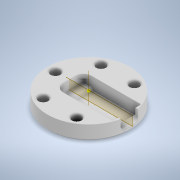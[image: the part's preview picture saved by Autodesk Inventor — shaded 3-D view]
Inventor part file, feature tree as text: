
AUTODESK INVENTOR PART (.ipt)
format: ipt  version: 2021 (Build 250183000, 183)  size: 815,104 bytes
history: native  units: in
note: dims shown in document units (in); Inventor stores cm internally (conversion verified against a paired STEP export)
features: sketch x8, extrude x6, fillet x4, chamfer x3, other x1, plane x1, pattern_circular x1, mirror x1
ambient origin geometry x8: Origin, YZ Plane, XZ Plane, XY Plane, X Axis, Y Axis, Z Axis, Center Point
bodies: Solid1 (feature_tree)
feature tree (25):
  extrude  "Extrusion1"  Depth=0.3701in TaperAngle=0.0deg
  chamfer  "Chamfer2"  Distance=0.2441in
  extrude  "Extrusion2"  Depth=0.1417in
  extrude  "Extrusion3"  Depth=0.2181in
  other  "Work Axis1"
  plane  "Work Plane1"
  extrude  "Extrusion5"  Depth=0.8268in
  extrude  "Extrusion4"  Depth=0.3539in
  fillet  "Fillet4"  Radius=0.1969in
  pattern_circular  "Circular Pattern2"  [2 undecoded]
  fillet  "Fillet7"  Radius=0.1417in
  extrude  "Initals"  TaperAngle=0.0deg  [1 undecoded]
  fillet  "Fillet9"  [1 undecoded]
  fillet  "Fillet10"  Radius=0.0394in
  mirror  "Mirror6"
  sketch  "Sketch18"  dims[d18=0.2047in d19=0.0in d23=0.8268in d24=0.3539in d31=0.1969in d32=0.063in d33=0.0in d44=0.1417in d47=0.0in d48=0.0in d49=0.0in d51=0.0in d54=0.0551in d55=0.0in d56=45.0deg d58=0.0394in d59=0.1181in d60=1.9685in d61=240.0deg d72=0.0315in d80=1.1811in d81=0.5906in d82=0.9728in d83=0.4864in d84=0.0394in d85=0.0in d86=0.547in d87=0.2735in d88=0.0787in d89=0.0in d90=0.0787in d98=0.1024in d99=0.0in d100=0.0in d101=0.2362in d102=0.0315in d103=0.0315in d104=0.2953in d105=0.1575in d106=0.1969in d107=0.063in d108=0.0787in d109=45.0deg d110=0.063in d111=0.0787in d112=45.0deg d91=0.0197in d92=0.0344in d93=0.0197in d94=0.0344in d120=0.0197in d121=0.0344in d122=0.0197in d123=0.0344in]
  chamfer  "Chamfer4"  Distance=0.1181in Angle=240.0deg
  chamfer  "Chamfer5"  Distance=0.0315in
  sketch  "Sketch1"  dims[d0=2.0472in d3=0.3701in d4=0.0in]
  sketch  "Sketch2"  dims[d5=1.4315in]
  sketch  "Sketch3"  dims[d6=0.7079in]
  sketch  "Sketch4"  dims[d7=0.3539in]
  sketch  "Sketch7"  dims[d8=0.4882in d9=0.2441in d10=0.0in]
  sketch  "Sketch12"  dims[d11=0.0in d14=0.1417in]
  sketch  "Sketch13"  dims[d15=0.0in d16=0.0in d17=0.2181in]
note: 4 required parameter values undecoded (feature->parameter linkage not recoverable at this tier; creation-order binding heuristic only, values carry confidence <= 0.55)
